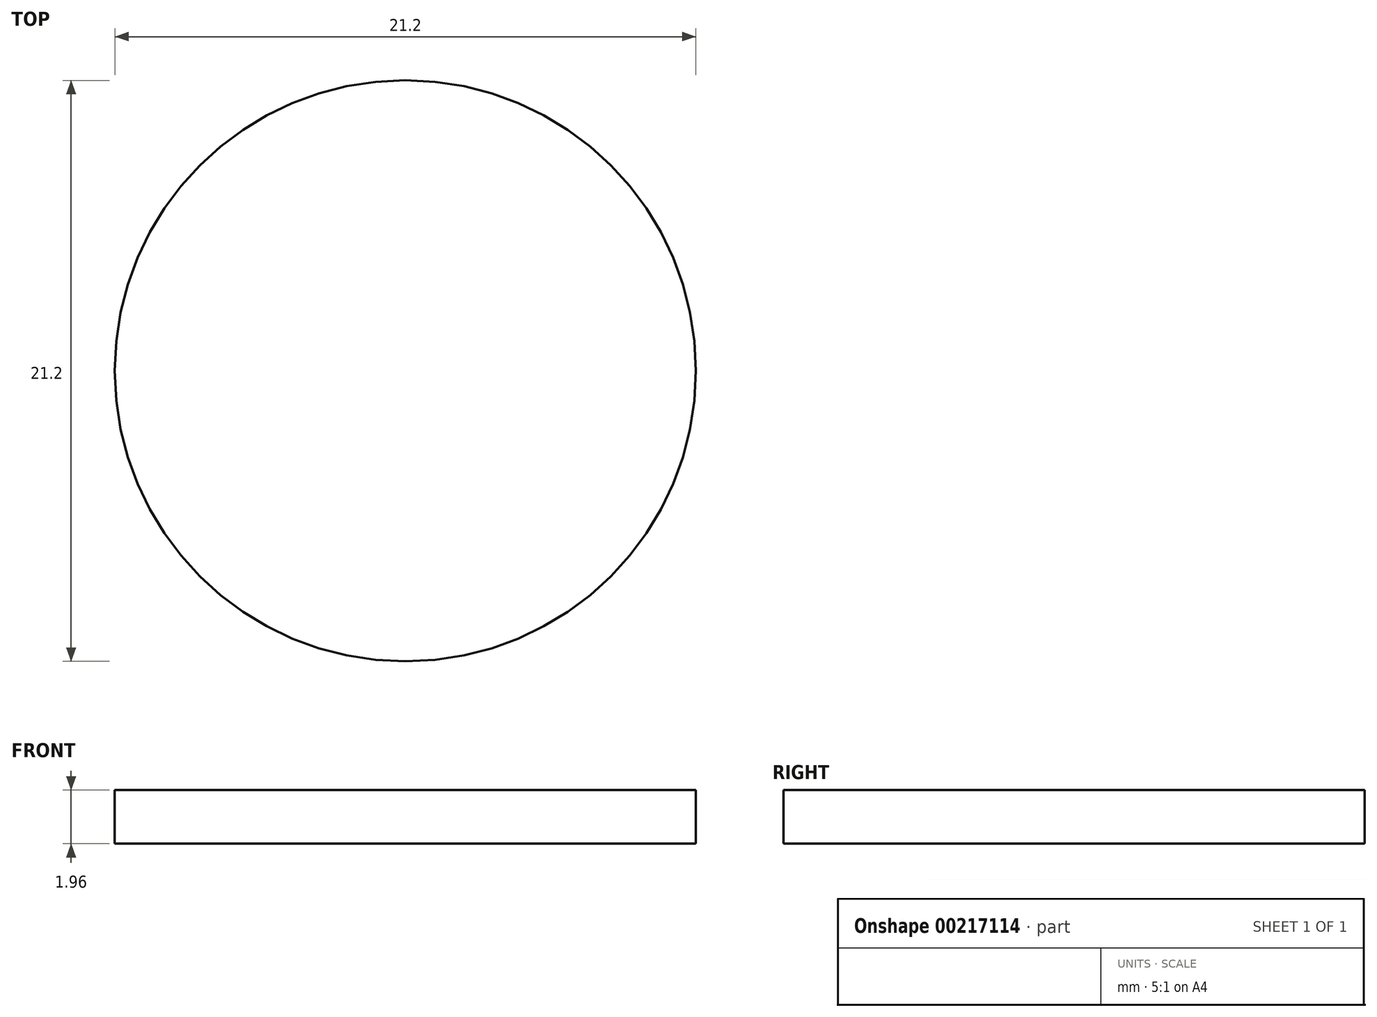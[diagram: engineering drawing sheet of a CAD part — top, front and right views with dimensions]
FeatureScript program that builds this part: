
annotation { "Feature Type Name" : "Feature", "Feature Type Description" : "" }
export const myFeature = defineFeature(function(context is Context, id is Id, definition is map)
    precondition{}
    {
        {
            var Q0;
            Q0=qCreatedBy(makeId("Top.planeOp"),FACE);
            var sketch = newSketch(context, id + "F0", { "sketchPlane" : qUnion([Q0])});
            skCircle(sketch, "E0", {"center": v(0, 0) * mm, "radius": 10.6 * mm});
            skSolve(sketch);
        }
        {
            var Q0;
            Q0 = qSketchRegion(id + "F0", true);
            extrude(context, id + "F1", {"entities" : qUnion([Q0]), "endBound" : BoundingType.SYMMETRIC, "depth" : 1.95 * mm});
        }
    });
